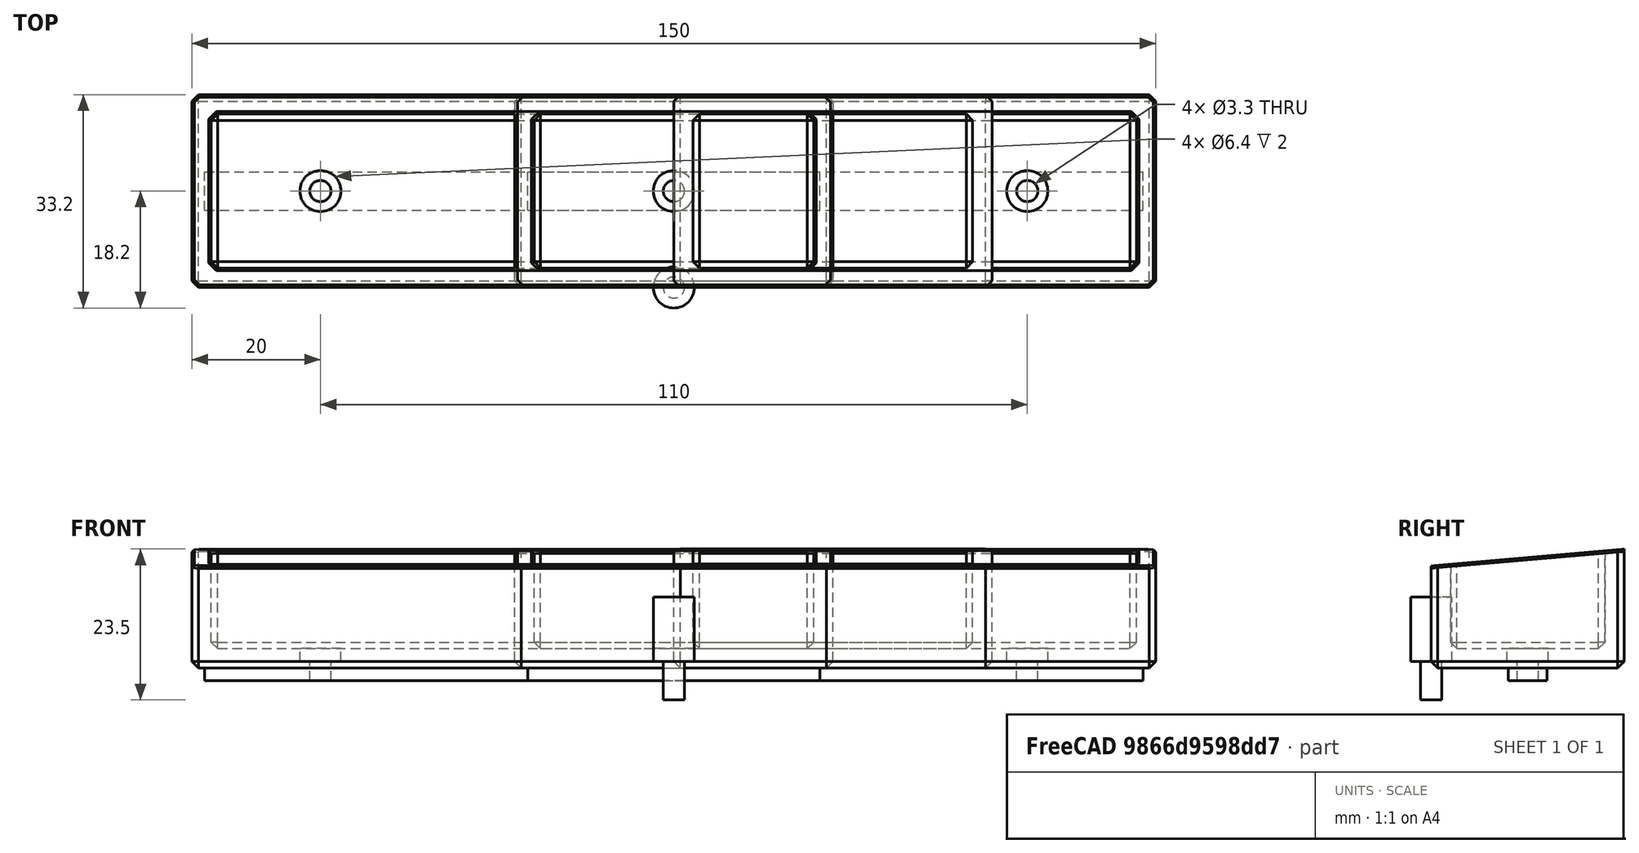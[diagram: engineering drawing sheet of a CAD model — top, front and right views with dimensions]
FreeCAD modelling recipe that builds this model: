
FCSTD DOCUMENT  (FreeCAD 0.18R16146 (Git))
Label: front-tray
License: All rights reserved
LicenseURL: http://en.wikipedia.org/wiki/All_rights_reserved
objects: Part::Box×7, Part::Feature×7, Part::MultiFuse×5, Part::Cut×4, Part::Chamfer×4, Part::MultiCommon×2, Part::Cylinder×2
note: 31 computed .brp shape members not serialized (recipe doc carries the construction recipe); baked Part::Feature solids carry a one-line shape summary decoded from their .brp

FEATURE [Part::Box] Box  label="Cube"
  AttacherType = Attacher::AttachEngine3D
  Height = 30
  Length = 150
  Width = 30
FEATURE [Part::Box] Box001  label="Cube001"
  AttacherType = Attacher::AttachEngine3D
  Height = 30
  Length = 144
  Placement = pos=(3,3,3) rot=(0,0,1;0rad)
  Width = 24
FEATURE [Part::Cut] Cut
  Base = -> Box
  Tool = -> Box001
FEATURE [Part::Chamfer] Chamfer
  Base = -> Cut
  Edges = 8 edges r=1: [Edge17,Edge18,Edge19,Edge20,Edge21,Edge22,Edge23,Edge24]
FEATURE [Part::Chamfer] Chamfer001
  Base = -> Chamfer
  Edges = 8 edges r=1: [Edge29,Edge30,Edge31,Edge32,Edge33,Edge34,Edge35,Edge36]
FEATURE [Part::Box] Box002  label="Cube002"
  AttacherType = Attacher::AttachEngine3D
  Height = 20
  Length = 160
  Placement = pos=(-5,-10,15) rot=(1,0,0;0.087266rad)
  Width = 60
FEATURE [Part::Cut] Cut001
  Base = -> Chamfer001
  Tool = -> Box002
FEATURE [Part::Feature] Cut001001  label="Cut002"
  shape: bbox 150 x 30 x 18.5 mm, 35 faces (baked)
FEATURE [Part::Feature] Cut001002  label="Cut003"
  shape: bbox 150 x 30 x 18.5 mm, 35 faces (baked)
FEATURE [Part::Box] Box003  label="Cube003"
  AttacherType = Attacher::AttachEngine3D
  Height = 21
  Length = 25
  Width = 34
FEATURE [Part::Box] Box004  label="Cube004"
  AttacherType = Attacher::AttachEngine3D
  Height = 21
  Length = 25
  Placement = pos=(125,0,0) rot=(0,0,1;0rad)
  Width = 34
FEATURE [Part::MultiCommon] Common
  Placement = pos=(-100.5,0,0) rot=(0,0,1;0rad)
  Shapes = -> [Cut001001,Box004]
FEATURE [Part::MultiCommon] Common001
  Shapes = -> [Cut001002,Box003]
FEATURE [Part::MultiFuse] Fusion
  Shapes = -> [Common,Common001]
FEATURE [Part::Feature] Fusion001
  shape: bbox 49.5 x 30 x 18.5 mm, 35 faces (baked)
FEATURE [Part::Chamfer] Chamfer002
  Base = -> Fusion001
  Edges = 16 edges r=0.4: [Edge3,Edge5,Edge10,Edge16,Edge17,Edge18,Edge19,Edge20,Edge21,Edge22,Edge23,Edge24,Edge25,Edge26,Edge27,Edge28]
  Placement = pos=(-24.75,0,0) rot=(0,0,1;0rad)
FEATURE [Part::Chamfer] Chamfer003
  Base = -> Cut001
  Edges = 16 edges r=0.4: [Edge1,Edge5,Edge6,Edge7,Edge8,Edge9,Edge10,Edge11,Edge12,Edge13,Edge14,Edge15,Edge16,Edge17,Edge18,Edge19]
  Placement = pos=(-75,0,0) rot=(0,0,1;0rad)
FEATURE [Part::Box] Box005  label="Cube005"
  AttacherType = Attacher::AttachEngine3D
  Height = 2
  Length = 45.5
  Placement = pos=(-22.75,12,-2) rot=(0,0,1;0rad)
  Width = 6
FEATURE [Part::Box] Box008  label="Cube008"
  AttacherType = Attacher::AttachEngine3D
  Height = 2
  Length = 146
  Placement = pos=(-73,12,-2) rot=(0,0,1;0rad)
  Width = 6
FEATURE [Part::MultiFuse] Fusion002
  Shapes = -> [Chamfer002,Box005]
FEATURE [Part::MultiFuse] Fusion003
  Shapes = -> [Chamfer003,Box008]
FEATURE [Part::Cylinder] Cylinder
  Angle = 360
  AttacherType = Attacher::AttachEngine3D
  Height = 10
  Placement = pos=(0,0,-5) rot=(0,0,1;0rad)
  Radius = 1.65
FEATURE [Part::Cylinder] Cylinder001
  Angle = 360
  AttacherType = Attacher::AttachEngine3D
  Height = 10
  Placement = pos=(0,0,1) rot=(0,0,1;0rad)
  Radius = 3.2
FEATURE [Part::MultiFuse] Fusion004  label="m3"
  Shapes = -> [Cylinder001,Cylinder]
FEATURE [Part::Feature] Fusion004001  label="m004"
  Placement = pos=(0,15,0) rot=(0,0,1;0rad)
  shape: bbox 6.4 x 6.4 x 16 mm, 5 faces (baked)
FEATURE [Part::Feature] Fusion004002  label="m005"
  Placement = pos=(-55,15,0) rot=(0,0,1;0rad)
  shape: bbox 6.4 x 6.4 x 16 mm, 5 faces (baked)
FEATURE [Part::Feature] Fusion004003  label="m006"
  Placement = pos=(55,15,0) rot=(0,0,1;0rad)
  shape: bbox 6.4 x 6.4 x 16 mm, 5 faces (baked)
FEATURE [Part::Feature] Fusion004004  label="m007"
  Placement = pos=(0,15,0) rot=(0,0,1;0rad)
  shape: bbox 6.4 x 6.4 x 16 mm, 5 faces (baked)
FEATURE [Part::MultiFuse] Fusion004005
  Shapes = -> [Fusion004003,Fusion004002,Fusion004001]
FEATURE [Part::Cut] Cut001003  label="150mm"
  Base = -> Fusion003
  Tool = -> Fusion004005
FEATURE [Part::Cut] Cut001004  label="50mm"
  Base = -> Fusion002
  Tool = -> Fusion004004
